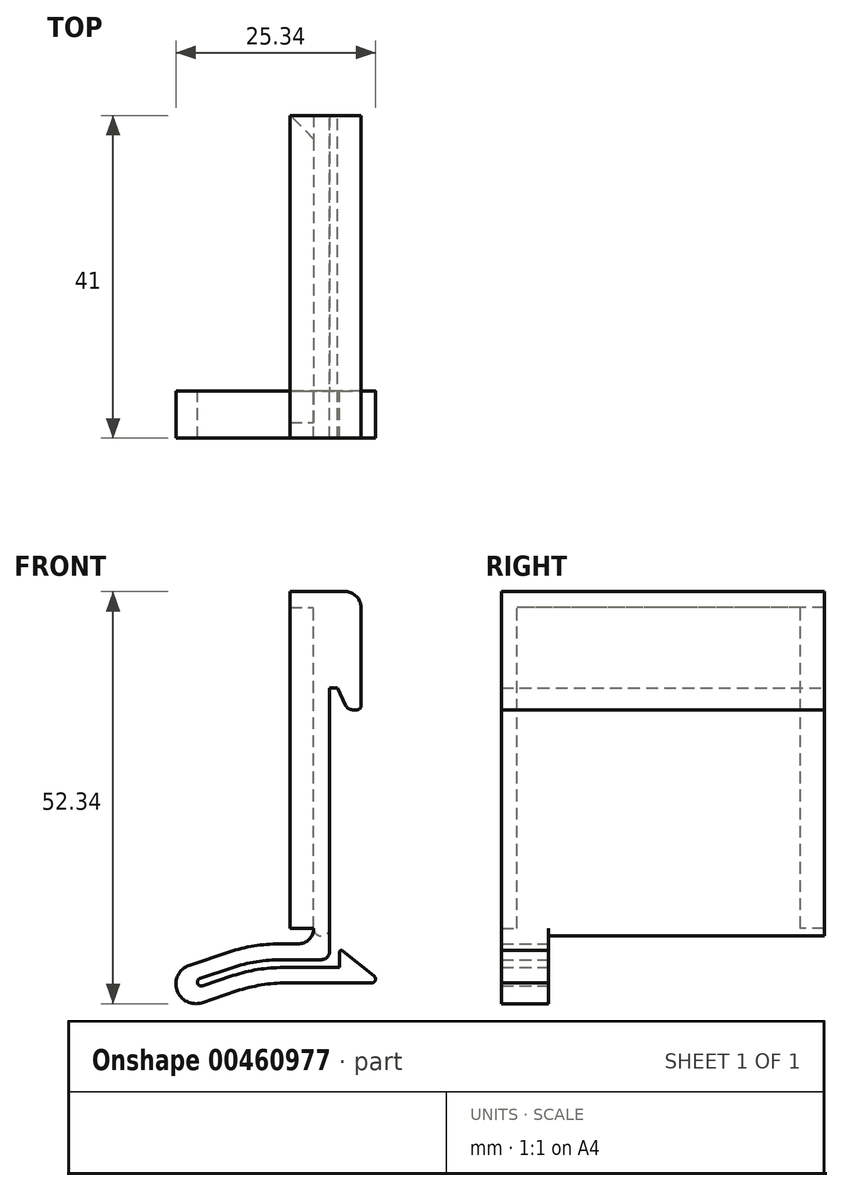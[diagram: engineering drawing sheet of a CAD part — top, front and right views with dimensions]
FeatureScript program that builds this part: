
annotation { "Feature Type Name" : "Feature", "Feature Type Description" : "" }
export const myFeature = defineFeature(function(context is Context, id is Id, definition is map)
    precondition{}
    {
        {
            var Q0;
            Q0=qCreatedBy(makeId("Front.planeOp"),FACE);
            var sketch = newSketch(context, id + "F0", { "sketchPlane" : qUnion([Q0])});
            skLineSegment(sketch, "E0", {"start": v(14.5, 14) * mm, "end": v(14.5, 10) * mm});
            skArc(sketch, "E1", {"start": v(18, 11.5) * mm, "mid": v(18.35, 11.65) * mm, "end": v(18.5, 12) * mm});
            skArc(sketch, "E2", {"start": v(18.5, 24.5) * mm, "mid": v(17.91, 25.91) * mm, "end": v(16.5, 26.5) * mm});
            skLineSegment(sketch, "E3", {"start": v(18.5, 24.5) * mm, "end": v(18.5, 12) * mm});
            skLineSegment(sketch, "E4", {"start": v(14.5, 14.25) * mm, "end": v(15.5, 14.25) * mm});
            skLineSegment(sketch, "E5", {"start": v(15.75, -21.25) * mm, "end": v(15.75, -19.32) * mm});
            skArc(sketch, "E6", {"start": v(16.15, -19.12) * mm, "mid": v(15.9, -19.1) * mm, "end": v(15.75, -19.32) * mm});
            skLineSegment(sketch, "E7", {"start": v(14.5, -19.25) * mm, "end": v(14.5, 14.25) * mm});
            skArc(sketch, "E8", {"start": v(9.03, -23.21) * mm, "mid": v(5.83, -23.47) * mm, "end": v(2.7, -24.24) * mm});
            skArc(sketch, "E9", {"start": v(8.6, -21.25) * mm, "mid": v(5.39, -21.5) * mm, "end": v(2.27, -22.28) * mm});
            skArc(sketch, "E10", {"start": v(8.43, -20.25) * mm, "mid": v(5.23, -20.5) * mm, "end": v(2.1, -21.28) * mm});
            skArc(sketch, "E11", {"start": v(-1.95, -22.63) * mm, "mid": v(-2.26, -23.26) * mm, "end": v(-1.63, -23.58) * mm});
            skArc(sketch, "E12", {"start": v(13.5, -20.25) * mm, "mid": v(14.2, -19.96) * mm, "end": v(14.5, -19.25) * mm});
            skLineSegment(sketch, "E13", {"start": v(15.75, -21.25) * mm, "end": v(8.6, -21.25) * mm});
            skLineSegment(sketch, "E14", {"start": v(2.27, -22.28) * mm, "end": v(-1.63, -23.58) * mm});
            skLineSegment(sketch, "E15", {"start": v(13.5, -20.25) * mm, "end": v(8.43, -20.25) * mm});
            skLineSegment(sketch, "E16", {"start": v(2.1, -21.28) * mm, "end": v(-1.95, -22.63) * mm});
            skLineSegment(sketch, "E17", {"start": v(2.7, -24.24) * mm, "end": v(-1.7, -25.71) * mm});
            skLineSegment(sketch, "E18", {"start": v(9.03, -23.21) * mm, "end": v(19.84, -23.21) * mm});
            skLineSegment(sketch, "E19", {"start": v(20.15, -22.32) * mm, "end": v(16.15, -19.12) * mm});
            skArc(sketch, "E20", {"start": v(19.84, -23.21) * mm, "mid": v(20.3, -22.88) * mm, "end": v(20.15, -22.32) * mm});
            skLineSegment(sketch, "E21", {"start": v(15.5, 14.25) * mm, "end": v(16.54, 12.07) * mm});
            skLineSegment(sketch, "E22", {"start": v(17.44, 11.5) * mm, "end": v(18, 11.5) * mm});
            skArc(sketch, "E23", {"start": v(16.54, 12.07) * mm, "mid": v(16.9, 11.65) * mm, "end": v(17.44, 11.5) * mm});
            skArc(sketch, "E24", {"start": v(10.5, -18.25) * mm, "mid": v(11.91, -17.66) * mm, "end": v(12.5, -16.25) * mm});
            skLineSegment(sketch, "E25", {"start": v(12.5, 22.5) * mm, "end": v(12.5, -16.25) * mm});
            skLineSegment(sketch, "E26", {"start": v(10.5, -18.25) * mm, "end": v(8.1, -18.25) * mm});
            skArc(sketch, "E27", {"start": v(8.1, -18.25) * mm, "mid": v(4.9, -18.5) * mm, "end": v(1.78, -19.28) * mm});
            skArc(sketch, "E28", {"start": v(-18, 24.5) * mm, "mid": v(-19.41, 23.91) * mm, "end": v(-20, 22.5) * mm});
            skArc(sketch, "E29", {"start": v(-20, 26.5) * mm, "mid": v(-21.41, 25.91) * mm, "end": v(-22, 24.5) * mm});
            skLineSegment(sketch, "E30", {"start": v(1.78, -19.28) * mm, "end": v(-3.3, -20.97) * mm});
            skArc(sketch, "E31", {"start": v(-3.3, -20.97) * mm, "mid": v(-4.87, -24.13) * mm, "end": v(-1.7, -25.71) * mm});
            skLineSegment(sketch, "E32", {"start": v(12.5, 22.5) * mm, "end": v(12.5, 24.5) * mm});
            skLineSegment(sketch, "E33", {"start": v(16.5, 26.5) * mm, "end": v(14.5, 26.5) * mm});
            skLineSegment(sketch, "E34", {"start": v(12.5, 24.5) * mm, "end": v(12.5, 26.5) * mm});
            skLineSegment(sketch, "E35", {"start": v(14.5, 26.5) * mm, "end": v(12.5, 26.5) * mm});
            skSolve(sketch);
        }
        {
            var Q0;
            Q0=makeQuery(id+"F0.imprint","IMPRINT",FACE,{"disambiguationData":[TD([[makeQuery(id+"F0.imprint","IMPRINT",EDGE,{"derivedFrom":sQuery(id+"F0.wireOp",EDGE,"E1")}),1.0]])]});
            extrude(context, id + "F1", {"entities" : qUnion([Q0]), "depth" : 6 * mm});
        }
        {
            var Q0;
            Q0=makeQuery(id+"F1.opExtrude","CAP_FACE",FACE,{"disambiguationData":[OSD([sQuery(id+"F0.wireOp",EDGE,"E1"),sQuery(id+"F0.wireOp",EDGE,"E2"),sQuery(id+"F0.wireOp",EDGE,"E3"),sQuery(id+"F0.wireOp",EDGE,"E4"),sQuery(id+"F0.wireOp",EDGE,"E5"),sQuery(id+"F0.wireOp",EDGE,"E6"),sQuery(id+"F0.wireOp",EDGE,"E7"),sQuery(id+"F0.wireOp",EDGE,"E8"),sQuery(id+"F0.wireOp",EDGE,"E9"),sQuery(id+"F0.wireOp",EDGE,"E10"),sQuery(id+"F0.wireOp",EDGE,"E11"),sQuery(id+"F0.wireOp",EDGE,"E12"),sQuery(id+"F0.wireOp",EDGE,"E13"),sQuery(id+"F0.wireOp",EDGE,"E14"),sQuery(id+"F0.wireOp",EDGE,"E15"),sQuery(id+"F0.wireOp",EDGE,"E16"),sQuery(id+"F0.wireOp",EDGE,"E17"),sQuery(id+"F0.wireOp",EDGE,"E18"),sQuery(id+"F0.wireOp",EDGE,"E19"),sQuery(id+"F0.wireOp",EDGE,"E20"),sQuery(id+"F0.wireOp",EDGE,"E21"),sQuery(id+"F0.wireOp",EDGE,"E22"),sQuery(id+"F0.wireOp",EDGE,"E23"),sQuery(id+"F0.wireOp",EDGE,"E24"),sQuery(id+"F0.wireOp",EDGE,"E25"),sQuery(id+"F0.wireOp",EDGE,"E26"),sQuery(id+"F0.wireOp",EDGE,"E27"),sQuery(id+"F0.wireOp",EDGE,"E30"),sQuery(id+"F0.wireOp",EDGE,"E31"),sQuery(id+"F0.wireOp",EDGE,"E32"),sQuery(id+"F0.wireOp",EDGE,"E33"),sQuery(id+"F0.wireOp",EDGE,"hjyiXBsQ-mqfY-QnGN-1a3u-Cgr02i7tssEI")])],"isStart":true});
            var sketch = newSketch(context, id + "F2", { "sketchPlane" : qUnion([Q0])});
            skLineSegment(sketch, "E36", {"start": v(-54.25, -13.88) * mm, "end": v(-54.25, -17.88) * mm});
            skArc(sketch, "E37", {"start": v(-50.75, -16.38) * mm, "mid": v(-50.4, -16.24) * mm, "end": v(-50.25, -15.88) * mm});
            skArc(sketch, "E38", {"start": v(-50.25, -3.38) * mm, "mid": v(-50.83, -1.97) * mm, "end": v(-52.25, -1.38) * mm});
            skLineSegment(sketch, "E39", {"start": v(-50.25, -3.38) * mm, "end": v(-50.25, -15.88) * mm});
            skLineSegment(sketch, "E40", {"start": v(-54.25, -13.63) * mm, "end": v(-53.25, -13.63) * mm});
            skArc(sketch, "E41", {"start": v(-52.6, -47) * mm, "mid": v(-52.86, -46.98) * mm, "end": v(-53, -47.2) * mm});
            skLineSegment(sketch, "E42", {"start": v(-54.25, -47.13) * mm, "end": v(-54.25, -13.63) * mm});
            skLineSegment(sketch, "E43", {"start": v(-53.25, -13.63) * mm, "end": v(-52.2, -15.81) * mm});
            skLineSegment(sketch, "E44", {"start": v(-51.3, -16.38) * mm, "end": v(-50.75, -16.38) * mm});
            skArc(sketch, "E45", {"start": v(-52.2, -15.81) * mm, "mid": v(-51.84, -16.23) * mm, "end": v(-51.3, -16.38) * mm});
            skArc(sketch, "E46", {"start": v(-58.25, -46.13) * mm, "mid": v(-56.83, -45.55) * mm, "end": v(-56.25, -44.13) * mm});
            skLineSegment(sketch, "E47", {"start": v(-56.25, -5.38) * mm, "end": v(-56.25, -44.13) * mm});
            skLineSegment(sketch, "E48", {"start": v(-56.25, -5.38) * mm, "end": v(-56.25, -3.38) * mm});
            skLineSegment(sketch, "E49", {"start": v(-52.25, -1.38) * mm, "end": v(-54.25, -1.38) * mm});
            skArc(sketch, "E50", {"start": v(-54.25, -1.38) * mm, "mid": v(-55.66, -1.97) * mm, "end": v(-56.25, -3.38) * mm});
            skLineSegment(sketch, "E51.0", {"start": v(-12.5, -16.25) * mm, "end": v(-12.5, 24.5) * mm});
            skLineSegment(sketch, "E52.0", {"start": v(-14.5, -16.25) * mm, "end": v(-14.5, 14.25) * mm});
            skPoint(sketch, "E53.0", {"position": v(-15, 14.25) * mm});
            skLineSegment(sketch, "E54.0", {"start": v(-15.5, 14.25) * mm, "end": v(-16.54, 12.07) * mm});
            skLineSegment(sketch, "E55.0", {"start": v(-14.5, 14.25) * mm, "end": v(-15.5, 14.25) * mm});
            skArc(sketch, "E56.0", {"start": v(-16.54, 12.07) * mm, "mid": v(-16.9, 11.65) * mm, "end": v(-17.44, 11.5) * mm});
            skPoint(sketch, "E57.0", {"position": v(-17.72, 11.5) * mm});
            skLineSegment(sketch, "E58.0", {"start": v(-17.44, 11.5) * mm, "end": v(-18, 11.5) * mm});
            skArc(sketch, "E59.0", {"start": v(-18, 11.5) * mm, "mid": v(-18.35, 11.65) * mm, "end": v(-18.5, 12) * mm});
            skLineSegment(sketch, "E60.0", {"start": v(-18.5, 24.5) * mm, "end": v(-18.5, 12) * mm});
            skArc(sketch, "E61.0", {"start": v(-18.5, 24.5) * mm, "mid": v(-17.91, 25.91) * mm, "end": v(-16.5, 26.5) * mm});
            skLineSegment(sketch, "E62.0", {"start": v(-16.5, 26.5) * mm, "end": v(-16.5, 26.5) * mm});
            skArc(sketch, "E63", {"start": v(-14.5, -16.25) * mm, "mid": v(-13.5, -17.25) * mm, "end": v(-12.5, -16.25) * mm});
            skPoint(sketch, "E64.orphan", {"position": v(-14.5, -19.25) * mm});
            skLineSegment(sketch, "E65.0", {"start": v(-12.5, -16.25) * mm, "end": v(-12.5, 26.5) * mm});
            skLineSegment(sketch, "E66.0", {"start": v(-16.5, 26.5) * mm, "end": v(-12.5, 26.5) * mm});
            skSolve(sketch);
        }
        {
            var Q0;
            Q0=makeQuery(id+"F2.imprint","IMPRINT",FACE,{"disambiguationData":[TD([[makeQuery(id+"F2.imprint","IMPRINT",EDGE,{"derivedFrom":sQuery(id+"F2.wireOp",EDGE,"E52.0")}),-1.0]])]});
            extrude(context, id + "F3", {"entities" : qUnion([Q0]), "operationType" : NewBodyOperationType.ADD, "depth" : 35 * mm});
        }
        {
            var Q0;
            Q0=makeQuery(id+"F3.boolean.opBoolean","MERGE",FACE,{"derivedFrom":[makeQuery(id+"F1.opExtrude","SWEPT_FACE",FACE,{"disambiguationData":[OSD([sQuery(id+"F0.wireOp",EDGE,"E25"),sQuery(id+"F0.wireOp",EDGE,"E32"),sQuery(id+"F0.wireOp",EDGE,"E34")])]}),makeQuery(id+"F3.opExtrude","SWEPT_FACE",FACE,{"disambiguationData":[OSD([sQuery(id+"F2.wireOp",EDGE,"E65.0")])]})]});
            var sketch = newSketch(context, id + "F4", { "sketchPlane" : qUnion([Q0])});
            skLineSegment(sketch, "E67.top", {"start": v(-32, 24.5) * mm, "end": v(4, 24.5) * mm});
            skLineSegment(sketch, "E67.left", {"start": v(-32, -16.25) * mm, "end": v(-32, 24.5) * mm});
            skLineSegment(sketch, "E67.right", {"start": v(4, -16.25) * mm, "end": v(4, 24.5) * mm});
            skLineSegment(sketch, "E68.0", {"start": v(6, -16.25) * mm, "end": v(6, 26.5) * mm});
            skLineSegment(sketch, "E69.0", {"start": v(6, 26.5) * mm, "end": v(-35, 26.5) * mm});
            skLineSegment(sketch, "E70.0", {"start": v(-35, -16.25) * mm, "end": v(-35, 26.5) * mm});
            skLineSegment(sketch, "E71", {"start": v(-35, -16.25) * mm, "end": v(-32, -16.25) * mm});
            skLineSegment(sketch, "E72", {"start": v(4, -16.25) * mm, "end": v(6, -16.25) * mm});
            skSolve(sketch);
        }
        {
            var Q0;
            Q0 = qSketchRegion(id + "F4", true);
            extrude(context, id + "F5", {"entities" : qUnion([Q0]), "operationType" : NewBodyOperationType.ADD, "depth" : 3 * mm});
        }
        {
            var Q0;
            Q0=makeQuery(id+"F5.opExtrude","CAP_EDGE",EDGE,{"disambiguationData":[OSD([sQuery(id+"F4.wireOp",EDGE,"E67.left")])],"isStart":false});
            chamfer(context, id + "F6", {"entities" : qUnion([Q0]), "width" : 3 * mm, "tangentPropagation" : true});
        }
    });
